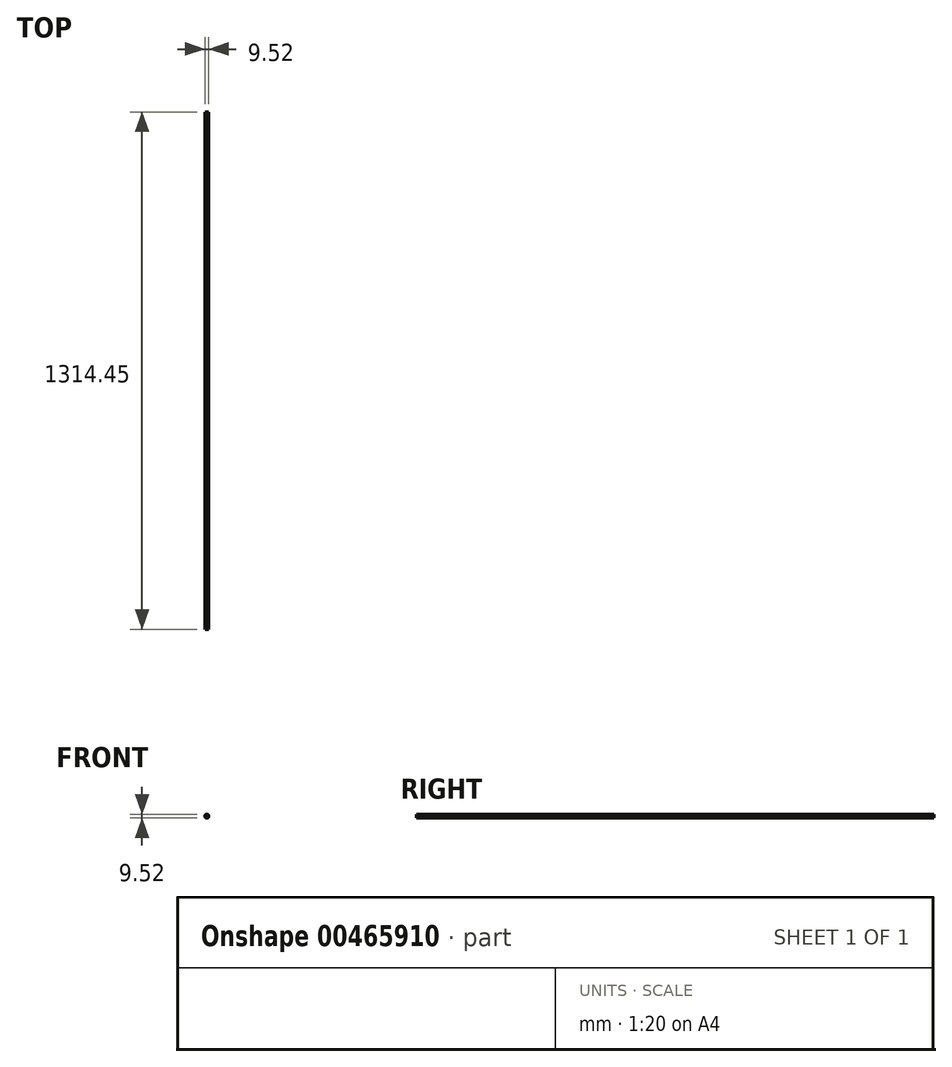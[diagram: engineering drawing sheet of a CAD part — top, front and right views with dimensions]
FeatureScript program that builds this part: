
annotation { "Feature Type Name" : "Feature", "Feature Type Description" : "" }
export const myFeature = defineFeature(function(context is Context, id is Id, definition is map)
    precondition{}
    {
        {
            var Q0;
            Q0=qCreatedBy(makeId("Front.planeOp"),FACE);
            var sketch = newSketch(context, id + "F0", { "sketchPlane" : qUnion([Q0])});
            skCircle(sketch, "E0", {"center": v(0, 0) * mm, "radius": 4.76 * mm});
            skSolve(sketch);
        }
        {
            var Q0;
            Q0=makeQuery(id+"F0.imprint","IMPRINT",FACE,{"disambiguationData":[TD([[makeQuery(id+"F0.imprint","IMPRINT",EDGE,{"derivedFrom":sQuery(id+"F0.wireOp",EDGE,"E0")}),1.0]])]});
            extrude(context, id + "F1", {"entities" : qUnion([Q0]), "depth" : 1314.45 * mm});
        }
    });
